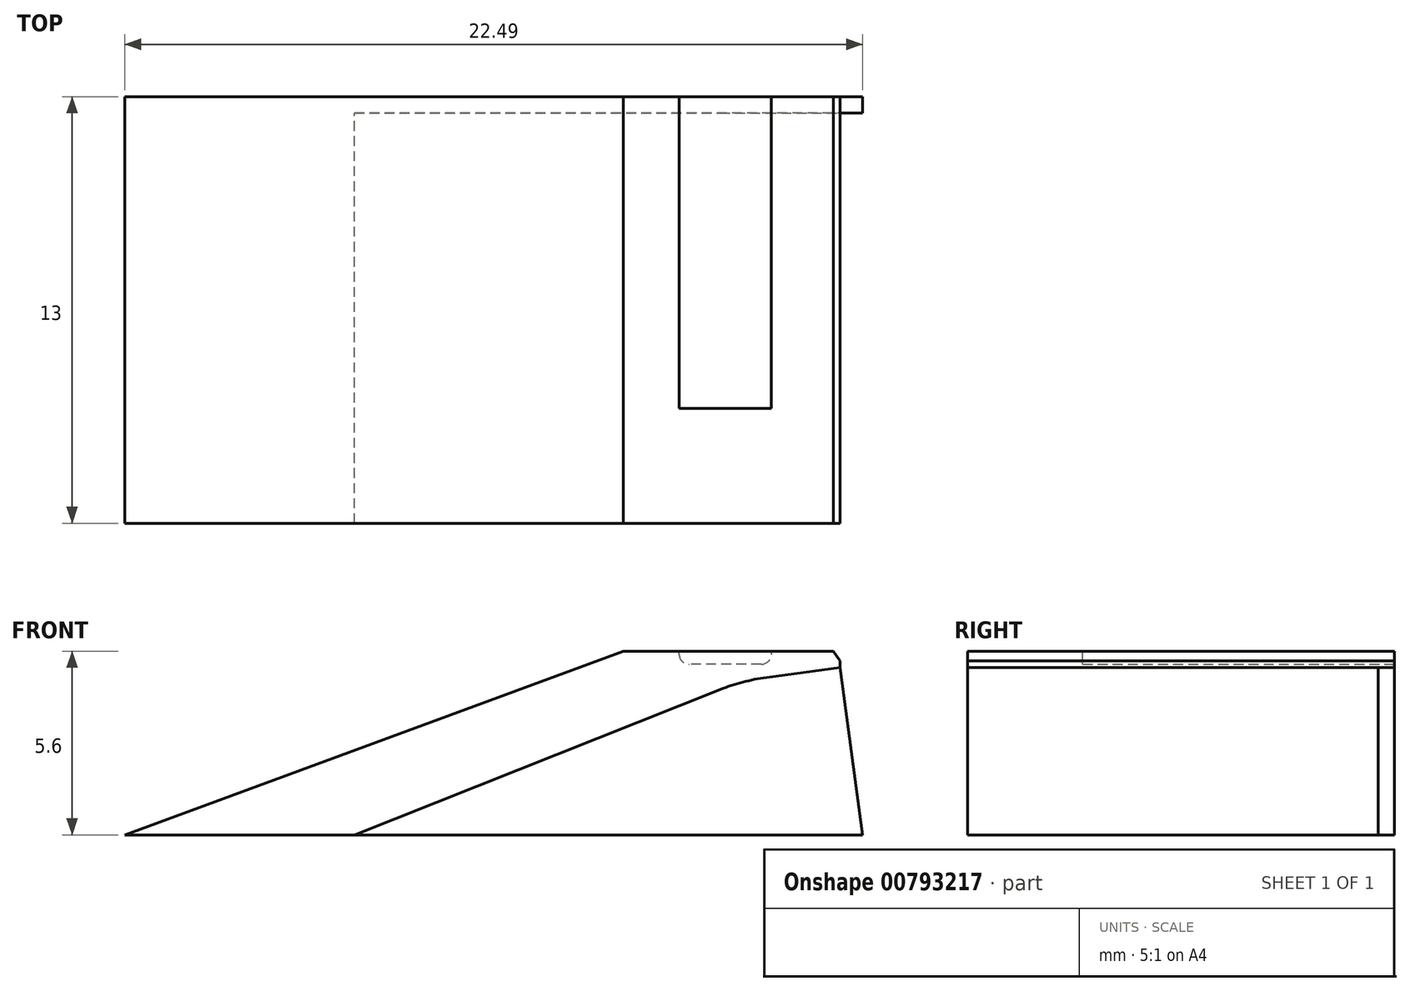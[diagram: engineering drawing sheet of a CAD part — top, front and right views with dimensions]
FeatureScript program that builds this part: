
annotation { "Feature Type Name" : "Feature", "Feature Type Description" : "" }
export const myFeature = defineFeature(function(context is Context, id is Id, definition is map)
    precondition{}
    {
        {
            var Q0;
            Q0=qCreatedBy(makeId("Front.planeOp"),FACE);
            var sketch = newSketch(context, id + "F0", { "sketchPlane" : qUnion([Q0])});
            skLineSegment(sketch, "E0", {"start": v(0, 0) * mm, "end": v(15.2, 5.6) * mm});
            skLineSegment(sketch, "E1", {"start": v(15.2, 5.6) * mm, "end": v(21.8, 5.6) * mm});
            skLineSegment(sketch, "E2", {"start": v(21.8, 5.6) * mm, "end": v(21.8, 5.1) * mm});
            skLineSegment(sketch, "E3", {"start": v(21.8, 5.1) * mm, "end": v(18.83, 4.7) * mm});
            skLineSegment(sketch, "E4", {"start": v(18.83, 4.7) * mm, "end": v(7, 0) * mm});
            skLineSegment(sketch, "E5", {"start": v(7, 0) * mm, "end": v(0, 0) * mm});
            skSolve(sketch);
        }
        {
            var Q0;
            Q0 = qSketchRegion(id + "F0", true);
            extrude(context, id + "F1", {"entities" : qUnion([Q0]), "endBound" : BoundingType.SYMMETRIC, "depth" : 13 * mm, "offsetDistance" : 25 * mm});
        }
        {
            var Q0;
            Q0=makeQuery(id+"F1.opExtrude","SWEPT_EDGE",EDGE,{"disambiguationData":[OSD([sQuery(id+"F0.wireOp",EDGE,"E3"),sQuery(id+"F0.wireOp",EDGE,"E4")])]});
            fillet(context, id + "F2", {"entities" : qUnion([Q0]), "radius" : 6 * mm, "tangentPropagation" : true, "allowEdgeOverflow" : false});
        }
        {
            var Q0;
            Q0=makeQuery(id+"F1.opExtrude","CAP_FACE",FACE,{"disambiguationData":[OSD([sQuery(id+"F0.wireOp",EDGE,"E0"),sQuery(id+"F0.wireOp",EDGE,"E1"),sQuery(id+"F0.wireOp",EDGE,"E2"),sQuery(id+"F0.wireOp",EDGE,"E3"),sQuery(id+"F0.wireOp",EDGE,"E4"),sQuery(id+"F0.wireOp",EDGE,"E5")])],"isStart":true});
            var sketch = newSketch(context, id + "F3", { "sketchPlane" : qUnion([Q0])});
            skLineSegment(sketch, "E6", {"start": v(-21.8, 5.1) * mm, "end": v(-22.49, 0) * mm});
            skLineSegment(sketch, "E7", {"start": v(-22.49, 0) * mm, "end": v(0, 0) * mm});
            skLineSegment(sketch, "E8", {"start": v(0, 0) * mm, "end": v(-15.2, 5.6) * mm});
            skLineSegment(sketch, "E9", {"start": v(-15.2, 5.6) * mm, "end": v(-21.8, 5.6) * mm});
            skLineSegment(sketch, "E10", {"start": v(-21.8, 5.6) * mm, "end": v(-21.8, 5.1) * mm});
            skSolve(sketch);
        }
        {
            var Q0;
            Q0 = qSketchRegion(id + "F3", true);
            extrude(context, id + "F4", {"entities" : qUnion([Q0]), "operationType" : NewBodyOperationType.ADD, "oppositeDirection" : true, "depth" : .5 * mm, "offsetDistance" : 25 * mm});
        }
        {
            var Q0;
            Q0=qCreatedBy(makeId("Front.planeOp"),FACE);
            var sketch = newSketch(context, id + "F5", { "sketchPlane" : qUnion([Q0])});
            skLineSegment(sketch, "E11", {"start": v(16.9, 5.6) * mm, "end": v(16.9, 5.2) * mm});
            skLineSegment(sketch, "E12", {"start": v(16.9, 5.2) * mm, "end": v(19.7, 5.2) * mm});
            skLineSegment(sketch, "E13", {"start": v(19.7, 5.2) * mm, "end": v(19.7, 5.6) * mm});
            skLineSegment(sketch, "E14", {"start": v(19.7, 5.6) * mm, "end": v(16.9, 5.6) * mm});
            skLineSegment(sketch, "E15", {"start": v(21.6, 5.6) * mm, "end": v(21.8, 5.3) * mm});
            skLineSegment(sketch, "E16", {"start": v(21.8, 5.3) * mm, "end": v(21.8, 5.6) * mm});
            skLineSegment(sketch, "E17", {"start": v(21.8, 5.6) * mm, "end": v(21.6, 5.6) * mm});
            skLineSegment(sketch, "E18", {"start": v(21.8, 5.6) * mm, "end": v(18.3, 5.6) * mm});
            skSolve(sketch);
        }
        {
            var Q0;
            Q0=makeQuery(id+"F5.imprint","IMPRINT",FACE,{"disambiguationData":[TD([[makeQuery(id+"F5.imprint","IMPRINT",EDGE,{"derivedFrom":sQuery(id+"F5.wireOp",EDGE,"E11")}),1.0]])]});
            extrude(context, id + "F6", {"entities" : qUnion([Q0]), "operationType" : NewBodyOperationType.REMOVE, "depth" : 3 * mm, "offsetDistance" : 25 * mm, "hasSecondDirection" : true, "secondDirectionOppositeDirection" : true, "secondDirectionDepth" : 25 * mm});
        }
        {
            var Q0;
            Q0=makeQuery(id+"F1.opExtrude","SWEPT_EDGE",EDGE,{"disambiguationData":[OSD([sQuery(id+"F0.wireOp",EDGE,"E1"),sQuery(id+"F0.wireOp",EDGE,"E2")])]});
            chamfer(context, id + "F7", {"entities" : qUnion([Q0]), "chamferType" : ChamferType.TWO_OFFSETS, "width1" : .2 * mm, "oppositeDirection" : false, "width2" : .3 * mm, "tangentPropagation" : true});
        }
        {
            var Q0;
            Q0=makeQuery(id+"F6.boolean.opBoolean","COPY",EDGE,{"derivedFrom":makeQuery(id+"F6.opExtrude","SWEPT_EDGE",EDGE,{"disambiguationData":[OSD([sQuery(id+"F5.wireOp",EDGE,"E11"),sQuery(id+"F5.wireOp",EDGE,"E12")])]})});
            var Q1;
            Q1=makeQuery(id+"F6.boolean.opBoolean","COPY",EDGE,{"derivedFrom":makeQuery(id+"F6.opExtrude","SWEPT_EDGE",EDGE,{"disambiguationData":[OSD([sQuery(id+"F5.wireOp",EDGE,"E12"),sQuery(id+"F5.wireOp",EDGE,"E13")])]})});
            fillet(context, id + "F8", {"entities" : qUnion([Q0, Q1]), "radius" : .3 * mm, "tangentPropagation" : true, "allowEdgeOverflow" : false});
        }
    });
